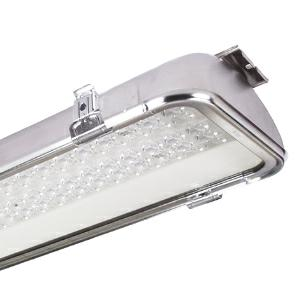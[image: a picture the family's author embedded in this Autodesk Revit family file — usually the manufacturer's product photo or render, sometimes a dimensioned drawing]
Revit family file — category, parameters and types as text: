
# Revit family: 3f_filippi_-_beta_235_93_vt_ampio_3f_filippi_-_52874_-_beta_235_led_932x40_ampio_vt_l1265
name_source: partatom
category: Lighting Fixtures
units: mm (PartAtom-declared; Revit-internal decimal feet)

## family parameters
Cut with Voids When Loaded = No
Host = Face
Light Source = No
Part Type = Normal
Room Calculation Point = No
Round Connector Dimension = Use Diameter
Shared = No

## types (1)
- 3F Filippi - Beta 235 93 VT Ampio (1 x LED, 12933 lm, 80 W, 4000 K)
    Apparent Load = 80 VA
    Approval mark = CE
    CIE Flux Codes = 55 92 99 100 100
    Color Rendering = 80
    Color Temperature = 4000 K
    Control Gear = Electronic ballast
    Default Elevation = 1800 mm
    Description = ILLUMINOTECHNICAL
Luminous efficiency 100% (DLOR 100%, ULOR 0%).
Initial luminous flux of the luminaire 12933 lm.
Wide symmetric distribution.
Installation Interdistance Transv.D = 1.18 x hu - Long.D = 1.19 x hu.
Tabular UGR (CIE 117 - 4H-8H; S=0.25H; 70/50/20): RUG 21.8 - 23.5.
Beam angle: 100° - 106°.
Luminous efficacy 162 lm/W.
Lifetime (L93/B10): 30000 h. (tq+25°C)
Lifetime (L90/B10): 50000 h. (tq+25°C)
Lifetime (L85/B10): 80000 h. (tq+25°C)
Lifetime (L80/B10): 100000 h. (tq+25°C)
Lifetime (L85/B10): 50000 h. (tq+45°C)
Sudden decreased luminous flux after 50000 hours: 0% (C0).
Photobiological safety in compliance with IEC/TR 62778: RG0 risk exempt, (IEC 62471).
In compliance with IEC/EN 62722-2-1 - IEC/EN 62717 standards.

SOURCE
2 linear LED modules 40W/840.
Energy efficiency class (UE 2019/2020 - UE 2019/2015): C.
CIE 13.3 Colour rendering index: CRI >80 (R9 <50%).
IES TM-30 Fidelity Index: Rf = 84 Rg = 95.
CCT nominal colour temperature 4000 K.
Colour initial tolerance (MacAdam): SDCM 3.

MECHANICAL
Housing in AISI 304 stainless steel, pressed in one single piece.
VT transparent glass, non-combustible, single-piece perimeter frame in stainless steel.
Oversized gear-tray reflector unit in highly reflective white painted hot-galvanised steel.
Methacrylate (PMMA) lenses with external flat surface.
Stainless steel snap-lock clips for diffuser mounting (safety n° 4 per fixture).
Luminaire with limited surface temperature. - D - (EN 60598-2-24)
Dimensions: 1265x235 mm, height 105 mm. Weight 9.42 kg.
IP65 protection degree.
Mechanical strength to impacts IK09 (10 joule).
Glow-wire test resistance 960°C.

ELECTRICAL
Halogen Free electronic wiring 230V-50/60Hz, power factor 0.95, THD <25%, constant output current, class I, 1 driver.
Power of the luminaire 80 W.
ENEC - CE.
Flicker: <4%.
Luminaire compliant with EN 60598-2-22 for power supply from a centralised emergency system CPSS (Central Power Supply System), not incorporated in the luminaire - high risk areas excluded. The default power and flux are 100% in AC and 100% in DC.
Ambient temperature from -20°C to +45°C.
Temperature class T6 max 85°C.
Quick connection via M20 3P connector with 9-13 mm tightening range.
Relative humidity UR: <85%.

INSTALLATION
Ceiling / Suspended / Wall.
All accessories dedicated to this product are available on the Catalog and on our website www.3F-Filippi.com.

APPLICATIONS
Dry, dusty indoor environments, subject to occasional water splashes.
Any environments except the ones where the luminaire materials are unsuitable.
Industrial environments, warehouses, environments where security locks are required on all clips, e.g. prisons (on request).
Environments in which it is necessary a total protection against falling fragments (eg environments with foodstuffs or machines with moving parts or with extreme temperature changes), use luminaires with laminated glass.
Tempered glass is not immune to falling fragments from harmless and caused by shocks or exceptionally derived from the tempering process.

WARNING
Fixture not suitable for cold stores with an ambient temperature <0°C and/or relative humidity >85%.
Luminaire designed for disposal/recycling at end-of-life.
Replaceable (LED only) light source by a professional. Replaceable control gear by a professional.
    Height = 105 mm
    Lamp = 1 x LED
    Lamp Light Flux = 12933 lm
    Lamp Power = 80 W
    Lamp count = 1
    Length = 1265 mm
    Lifetime = 50000 h
    Luminous efficacy = 162 lm/W
    Manufacturer = 3F Filippi
    ModVariant = No
    Model = 3F Filippi - 52874 - Beta 235 LED 932x40 AMPIO VT L1265
    Mounting Place = Ceiling
    Mounting Type = Pendant
    Number of Poles = 1
    OnlyDefault = Yes
    Power Factor = 1
    Product Name = 3F Filippi - Beta 235 93 VT Ampio
    Product group = pendant luminaire
    ProductGroupID = 9
    Protection Class = Protection class I
    Protection Degree = IP 65
    RLX_Detail_Level = 1
    RLX_Emergency_Light_Flux = 0 lm
    RLX_Emergency_Type = 0
    RLX_Emergency_Type_DB = No
    RlxData = <blob elided: 89421 chars, md5=a2c38ab3>
    Socket = socket
    Standby Power = 0 W
    System Light Flux = 12933 lm
    System Power = 80 W
    Type Comments = Product without accessories
    Type Image = 3ffilippi_52874.jpg
    URL = http://relux.com
    VarID = ---
    Voltage = 0 V
    Weight = 0.00 kg
    Width = 235 mm

## geometry (parser evidence)
native form markers: Blend x4, Sweep x12
no freeform markers — native parametric forms only
